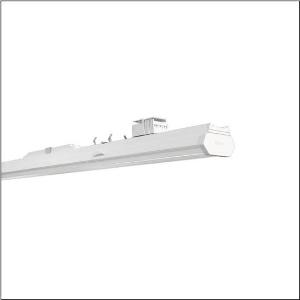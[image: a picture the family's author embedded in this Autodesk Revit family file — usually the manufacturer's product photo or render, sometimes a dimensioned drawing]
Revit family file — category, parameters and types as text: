
# Revit family: licross_11_protected_mo_51td1bdn68xg
name_source: partatom
category: Lighting Fixtures
units: mm (PartAtom-declared; Revit-internal decimal feet)

## family parameters
Cut with Voids When Loaded = No
Host = Face
Light Source = No
Part Type = Normal
Room Calculation Point = No
Round Connector Dimension = Use Diameter
Shared = No

## types (1)
- --- (1 x LED, 8310 lm, 51.3 W, 6500K)
    Apparent Load = 51 VA
    CIE Flux Codes = 54 82 95 97 100
    Color Rendering = 80
    Color Temperature = 6500K
    Default Elevation = 1800 mm
    Description = Licross 11 Protected MO, luminaire insert, of sheet steel, galvanised, coil coated, white, length: 1.500mm, width: 90mm, height: 101mm, LED rated luminous flux: 8.310lm, light colour: 865, SDCM (Standard Deviation of Colour Matching)MacAdam ≤ 2 SDCM (initial), control gear: DALI 2, with plug, 5-pole, with phase selection, mains connection: 220..240V, AC, 50/60Hz, rated input power: 51W, internal wiring halogen-free, primary optical cover: cover, of PMMA, light emission: direct distribution, primary light characteristic: symmetric, protection rating (complete): IP54, insulation class (complete): insulation class I (protective earthing), certification: CE, ENEC, VDE, UKCA, protection symbol: D if used in an environment with non-conductive dust loads with corresponding accessories, impact resistance: IK06, permissible ambient temperature for indoor applications: -25..+35°C, corresponds to IFS (International Featured Standards) requirements for safety and quality in the food industry, reducing of maximum allowable ambient temperature of 5°C with ceiling mounting, LABS conformity tested according to VDMA 24364:2018-05, The light source and the operating device comply with the requirements of the Ecodesign Regulation (EU) 2019/2020 and are replaceable in accordance with this regulation, packaging unit: 1 piece
    Height = 92 mm
    Lamp = 1 x LED
    Lamp Light Flux = 8310 lm
    Lamp Power = 51.3 W
    Lamp count = 1
    Length = 1500 mm
    Luminous efficacy = 162 lm/W
    Manufacturer = Siteco
    ModVariant = No
    Model = 51TD1BDN68XG
    Mounting Place = Ceiling
    Mounting Type = Pendant
    Number of Poles = 1
    OnlyDefault = Yes
    Power Factor = 1
    Product Name = Licross 11 Protected MO
    Product group = luminaire insert | ceiling pendant
    ProductGroupID = 901
    Protection Class = Protection class I
    Protection Degree = IP 54
    RLX_Detail_Level = 1
    RLX_Emergency_Light_Flux = 0 lm
    RLX_Emergency_Type = 0
    RLX_Emergency_Type_DB = No
    RlxData = <blob elided: 24661 chars, md5=5e2738f5>
    Socket = socket
    Standby Power = 0 W
    System Light Flux = 8310 lm
    System Power = 51 W
    Type Comments = factory setting: luminous flux: 100 % | dim-lin: 254 | 341 mA
    Type Image = l_1256145.jpg
    URL = http://relux.com
    VarID = @adj_057723
    Voltage = 0 V
    Weight = 0.00 kg
    Width = 88 mm

## geometry (parser evidence)
native form markers: Blend x4, Sweep x9
no freeform markers — native parametric forms only
